SOLIDWORKS PART (.sldprt)
format: sldprt  version: not decoded by parser v0  size: 96,256 bytes
history: native  units: mm
features: sketch x3, cut_extrude x2, material x1, plane x1, extrude x1 (+11 scaffold rows collapsed)
feature tree (19):
  scaffold x11  (default folders/planes/origin — collapsed)
  material  "Material <not specified>"
  plane  "Plane1"  Offset=0mm
  sketch  "Sketch1"
  extrude  "Boss-Extrude1"  Depth=6.35mm
  sketch  "Sketch2"  dims[D1=0.1065mm]
  cut_extrude  "Cut-Extrude1"  Depth=9.525mm
  sketch  "Sketch3"  dims[D1=~6.030828mm]
  cut_extrude  "Cut-Extrude2"  Depth=9.525mm
decode coverage: 5 of 6 modeling features carry decoded parameters
note: ~ marks probable driven/reference dimensions
note: suppression state not decoded; provenance and decode notes live in map.json
